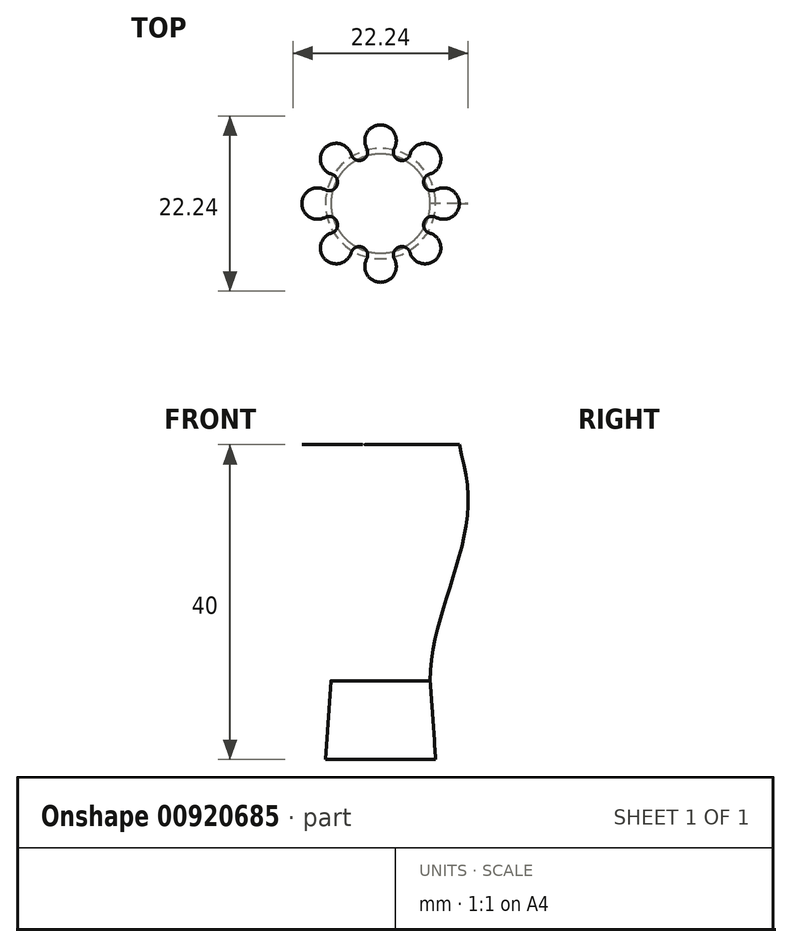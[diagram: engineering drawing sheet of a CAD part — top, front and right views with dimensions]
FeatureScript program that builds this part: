
annotation { "Feature Type Name" : "Feature", "Feature Type Description" : "" }
export const myFeature = defineFeature(function(context is Context, id is Id, definition is map)
    precondition{}
    {
        {
            var Q0;
            Q0=qCreatedBy(makeId("Front.planeOp"),FACE);
            var sketch = newSketch(context, id + "F0", { "sketchPlane" : qUnion([Q0])});
            skLineSegment(sketch, "E0", {"start": v(0, 0) * mm, "end": v(0, 33.9) * mm, "construction": true});
            skLineSegment(sketch, "E1", {"start": v(0, 0) * mm, "end": v(7, 0) * mm});
            skLineSegment(sketch, "E2", {"start": v(7, 0) * mm, "end": v(6.3, 10) * mm});
            skFitSpline(sketch, "E3", {"points": [v(6.3, 10) * mm, v(10, 40) * mm], "startDerivative": vector(-2.26, 32.38) * mm, "endDerivative": vector(-12.1, 32.97) * mm});
            skLineSegment(sketch, "E4", {"start": v(11.1, 33.89) * mm, "end": v(11.1, 17.48) * mm, "construction": true});
            skSolve(sketch);
        }
        {
            var Q0;
            Q0=qCreatedBy(makeId("Top.planeOp"),FACE);
            var Q1;
            Q1=sQuery(id+"F0.wireOp",VERTEX,"E2.end");
            cPlane(context, id + "F1", {"entities" : qUnion([Q0, Q1]), "cplaneType" : CPlaneType.PLANE_POINT, "offset" : 25 * mm, "width" : 150 * mm, "height" : 150 * mm});
        }
        {
            var Q0;
            Q0=qCreatedBy(makeId("Top.planeOp"),FACE);
            var Q1;
            Q1=sQuery(id+"F0.wireOp",VERTEX,"E4.start");
            cPlane(context, id + "F2", {"entities" : qUnion([Q0, Q1]), "cplaneType" : CPlaneType.PLANE_POINT, "offset" : 25 * mm, "width" : 150 * mm, "height" : 150 * mm});
        }
        {
            var Q0;
            Q0=qCreatedBy(makeId("Top.planeOp"),FACE);
            var Q1;
            Q1=sQuery(id+"F0.wireOp",VERTEX,"E3.end");
            cPlane(context, id + "F3", {"entities" : qUnion([Q0, Q1]), "cplaneType" : CPlaneType.PLANE_POINT, "offset" : 25 * mm, "width" : 150 * mm, "height" : 150 * mm});
        }
        {
            var Q0;
            Q0=qCreatedBy(makeId("Top.planeOp"),FACE);
            var sketch = newSketch(context, id + "F4", { "sketchPlane" : qUnion([Q0])});
            skCircle(sketch, "E5", {"center": v(0, 0) * mm, "radius": 7 * mm});
            skSolve(sketch);
        }
        {
            var Q0;
            Q0=qCreatedBy(id+"F1.planeOp",FACE);
            var sketch = newSketch(context, id + "F5", { "sketchPlane" : qUnion([Q0])});
            skCircle(sketch, "E6", {"center": v(0, 0) * mm, "radius": 6.3 * mm});
            skSolve(sketch);
        }
        {
            var Q0;
            Q0=qCreatedBy(id+"F3.planeOp",FACE);
            var sketch = newSketch(context, id + "F6", { "sketchPlane" : qUnion([Q0])});
            skCircle(sketch, "E7", {"center": v(0, 0) * mm, "radius": 10 * mm, "construction": true});
            skCircle(sketch, "E8", {"center": v(0, 0) * mm, "radius": 6 * mm, "construction": true});
            skLineSegment(sketch, "E9", {"start": v(0, 0) * mm, "end": v(12.38, 0) * mm, "construction": true});
            skLineSegment(sketch, "E10", {"start": v(0, 0) * mm, "end": v(10.76, 4.46) * mm, "construction": true});
            skArc(sketch, "E11", {"start": v(10, 0) * mm, "mid": v(9.02, 1.72) * mm, "end": v(7.05, 1.76) * mm});
            skArc(sketch, "E12", {"start": v(5.54, 2.3) * mm, "mid": v(6.18, 1.7) * mm, "end": v(7.05, 1.76) * mm});
            skArc(sketch, "E13.MirrorCS", {"start": v(5.54, -2.3) * mm, "mid": v(6.18, -1.7) * mm, "end": v(7.05, -1.76) * mm});
            skArc(sketch, "E14.MirrorCS", {"start": v(10, 0) * mm, "mid": v(9.02, -1.72) * mm, "end": v(7.05, -1.76) * mm});
            skArc(sketch, "E15.1.0", {"start": v(2.3, 5.54) * mm, "mid": v(3.17, 5.57) * mm, "end": v(3.74, 6.23) * mm});
            skArc(sketch, "E15.1.1", {"start": v(7.07, 7.07) * mm, "mid": v(5.17, 7.6) * mm, "end": v(3.74, 6.23) * mm});
            skArc(sketch, "E15.1.2", {"start": v(7.07, 7.07) * mm, "mid": v(7.6, 5.17) * mm, "end": v(6.23, 3.74) * mm});
            skArc(sketch, "E15.1.3", {"start": v(5.54, 2.3) * mm, "mid": v(5.57, 3.17) * mm, "end": v(6.23, 3.74) * mm});
            skArc(sketch, "E15.2.0", {"start": v(-2.3, 5.54) * mm, "mid": v(-1.7, 6.18) * mm, "end": v(-1.76, 7.05) * mm});
            skArc(sketch, "E15.2.1", {"start": v(0, 10) * mm, "mid": v(-1.72, 9.02) * mm, "end": v(-1.76, 7.05) * mm});
            skArc(sketch, "E15.2.2", {"start": v(0, 10) * mm, "mid": v(1.72, 9.02) * mm, "end": v(1.76, 7.05) * mm});
            skArc(sketch, "E15.2.3", {"start": v(2.3, 5.54) * mm, "mid": v(1.7, 6.18) * mm, "end": v(1.76, 7.05) * mm});
            skArc(sketch, "E15.3.0", {"start": v(-5.54, 2.3) * mm, "mid": v(-5.57, 3.17) * mm, "end": v(-6.23, 3.74) * mm});
            skArc(sketch, "E15.3.1", {"start": v(-7.07, 7.07) * mm, "mid": v(-7.6, 5.17) * mm, "end": v(-6.23, 3.74) * mm});
            skArc(sketch, "E15.3.2", {"start": v(-7.07, 7.07) * mm, "mid": v(-5.17, 7.6) * mm, "end": v(-3.74, 6.23) * mm});
            skArc(sketch, "E15.3.3", {"start": v(-2.3, 5.54) * mm, "mid": v(-3.17, 5.57) * mm, "end": v(-3.74, 6.23) * mm});
            skArc(sketch, "E15.4.0", {"start": v(-5.54, -2.3) * mm, "mid": v(-6.18, -1.7) * mm, "end": v(-7.05, -1.76) * mm});
            skArc(sketch, "E15.4.1", {"start": v(-10, 0) * mm, "mid": v(-9.02, -1.72) * mm, "end": v(-7.05, -1.76) * mm});
            skArc(sketch, "E15.4.2", {"start": v(-10, 0) * mm, "mid": v(-9.02, 1.72) * mm, "end": v(-7.05, 1.76) * mm});
            skArc(sketch, "E15.4.3", {"start": v(-5.54, 2.3) * mm, "mid": v(-6.18, 1.7) * mm, "end": v(-7.05, 1.76) * mm});
            skArc(sketch, "E15.5.0", {"start": v(-2.3, -5.54) * mm, "mid": v(-3.17, -5.57) * mm, "end": v(-3.74, -6.23) * mm});
            skArc(sketch, "E15.5.1", {"start": v(-7.07, -7.07) * mm, "mid": v(-5.17, -7.6) * mm, "end": v(-3.74, -6.23) * mm});
            skArc(sketch, "E15.5.2", {"start": v(-7.07, -7.07) * mm, "mid": v(-7.6, -5.17) * mm, "end": v(-6.23, -3.74) * mm});
            skArc(sketch, "E15.5.3", {"start": v(-5.54, -2.3) * mm, "mid": v(-5.57, -3.17) * mm, "end": v(-6.23, -3.74) * mm});
            skArc(sketch, "E15.6.0", {"start": v(2.3, -5.54) * mm, "mid": v(1.7, -6.18) * mm, "end": v(1.76, -7.05) * mm});
            skArc(sketch, "E15.6.1", {"start": v(0, -10) * mm, "mid": v(1.72, -9.02) * mm, "end": v(1.76, -7.05) * mm});
            skArc(sketch, "E15.6.2", {"start": v(0, -10) * mm, "mid": v(-1.72, -9.02) * mm, "end": v(-1.76, -7.05) * mm});
            skArc(sketch, "E15.6.3", {"start": v(-2.3, -5.54) * mm, "mid": v(-1.7, -6.18) * mm, "end": v(-1.76, -7.05) * mm});
            skArc(sketch, "E15.7.0", {"start": v(5.54, -2.3) * mm, "mid": v(5.57, -3.17) * mm, "end": v(6.23, -3.74) * mm});
            skArc(sketch, "E15.7.1", {"start": v(7.07, -7.07) * mm, "mid": v(7.6, -5.17) * mm, "end": v(6.23, -3.74) * mm});
            skArc(sketch, "E15.7.2", {"start": v(7.07, -7.07) * mm, "mid": v(5.17, -7.6) * mm, "end": v(3.74, -6.23) * mm});
            skArc(sketch, "E15.7.3", {"start": v(2.3, -5.54) * mm, "mid": v(3.17, -5.57) * mm, "end": v(3.74, -6.23) * mm});
            skSolve(sketch);
        }
        {
            var Q0;
            Q0=qCreatedBy(id+"F2.planeOp",FACE);
            var sketch = newSketch(context, id + "F7", { "sketchPlane" : qUnion([Q0])});
            skCircle(sketch, "E16", {"center": v(0, 0) * mm, "radius": 11.1 * mm, "construction": true});
            skCircle(sketch, "E17", {"center": v(0, 0) * mm, "radius": 7.1 * mm, "construction": true});
            skCircle(sketch, "E18.0", {"center": v(0, 0) * mm, "radius": 10 * mm, "construction": true});
            skCircle(sketch, "E19.0", {"center": v(0, 0) * mm, "radius": 6 * mm, "construction": true});
            skLineSegment(sketch, "E20", {"start": v(0, 10) * mm, "end": v(0, 11.1) * mm, "construction": true});
            skLineSegment(sketch, "E21", {"start": v(0, 6) * mm, "end": v(0, 7.1) * mm, "construction": true});
            skArc(sketch, "E22", {"start": v(11.1, 0) * mm, "mid": v(10.25, 1.63) * mm, "end": v(8.42, 1.88) * mm});
            skArc(sketch, "E23", {"start": v(6.55, 2.71) * mm, "mid": v(7.32, 1.93) * mm, "end": v(8.42, 1.88) * mm});
            skLineSegment(sketch, "E24.0", {"start": v(0, 0) * mm, "end": v(10.76, 4.46) * mm, "construction": true});
            skLineSegment(sketch, "E25.0", {"start": v(0, 0) * mm, "end": v(12.38, 0) * mm, "construction": true});
            skArc(sketch, "E26.MirrorCS", {"start": v(11.1, 0) * mm, "mid": v(10.25, -1.63) * mm, "end": v(8.42, -1.88) * mm});
            skArc(sketch, "E27.MirrorCS", {"start": v(6.55, -2.71) * mm, "mid": v(7.32, -1.93) * mm, "end": v(8.42, -1.88) * mm});
            skArc(sketch, "E28.1.0", {"start": v(2.71, 6.55) * mm, "mid": v(3.82, 6.54) * mm, "end": v(4.62, 7.29) * mm});
            skArc(sketch, "E28.1.1", {"start": v(7.84, 7.84) * mm, "mid": v(6.1, 8.4) * mm, "end": v(4.62, 7.29) * mm});
            skArc(sketch, "E28.1.2", {"start": v(7.84, 7.84) * mm, "mid": v(8.4, 6.1) * mm, "end": v(7.29, 4.62) * mm});
            skArc(sketch, "E28.1.3", {"start": v(6.55, 2.71) * mm, "mid": v(6.54, 3.82) * mm, "end": v(7.29, 4.62) * mm});
            skArc(sketch, "E28.2.0", {"start": v(-2.71, 6.55) * mm, "mid": v(-1.93, 7.32) * mm, "end": v(-1.88, 8.42) * mm});
            skArc(sketch, "E28.2.1", {"start": v(0, 11.1) * mm, "mid": v(-1.63, 10.25) * mm, "end": v(-1.88, 8.42) * mm});
            skArc(sketch, "E28.2.2", {"start": v(0, 11.1) * mm, "mid": v(1.63, 10.25) * mm, "end": v(1.88, 8.42) * mm});
            skArc(sketch, "E28.2.3", {"start": v(2.71, 6.55) * mm, "mid": v(1.93, 7.32) * mm, "end": v(1.88, 8.42) * mm});
            skArc(sketch, "E28.3.0", {"start": v(-6.55, 2.71) * mm, "mid": v(-6.54, 3.82) * mm, "end": v(-7.29, 4.62) * mm});
            skArc(sketch, "E28.3.1", {"start": v(-7.84, 7.84) * mm, "mid": v(-8.4, 6.1) * mm, "end": v(-7.29, 4.62) * mm});
            skArc(sketch, "E28.3.2", {"start": v(-7.84, 7.84) * mm, "mid": v(-6.1, 8.4) * mm, "end": v(-4.62, 7.29) * mm});
            skArc(sketch, "E28.3.3", {"start": v(-2.71, 6.55) * mm, "mid": v(-3.82, 6.54) * mm, "end": v(-4.62, 7.29) * mm});
            skArc(sketch, "E28.4.0", {"start": v(-6.55, -2.71) * mm, "mid": v(-7.32, -1.93) * mm, "end": v(-8.42, -1.88) * mm});
            skArc(sketch, "E28.4.1", {"start": v(-11.1, 0) * mm, "mid": v(-10.25, -1.63) * mm, "end": v(-8.42, -1.88) * mm});
            skArc(sketch, "E28.4.2", {"start": v(-11.1, 0) * mm, "mid": v(-10.25, 1.63) * mm, "end": v(-8.42, 1.88) * mm});
            skArc(sketch, "E28.4.3", {"start": v(-6.55, 2.71) * mm, "mid": v(-7.32, 1.93) * mm, "end": v(-8.42, 1.88) * mm});
            skArc(sketch, "E28.5.0", {"start": v(-2.71, -6.55) * mm, "mid": v(-3.82, -6.54) * mm, "end": v(-4.62, -7.29) * mm});
            skArc(sketch, "E28.5.1", {"start": v(-7.84, -7.84) * mm, "mid": v(-6.1, -8.4) * mm, "end": v(-4.62, -7.29) * mm});
            skArc(sketch, "E28.5.2", {"start": v(-7.84, -7.84) * mm, "mid": v(-8.4, -6.1) * mm, "end": v(-7.29, -4.62) * mm});
            skArc(sketch, "E28.5.3", {"start": v(-6.55, -2.71) * mm, "mid": v(-6.54, -3.82) * mm, "end": v(-7.29, -4.62) * mm});
            skArc(sketch, "E28.6.0", {"start": v(2.71, -6.55) * mm, "mid": v(1.93, -7.32) * mm, "end": v(1.88, -8.42) * mm});
            skArc(sketch, "E28.6.1", {"start": v(0, -11.1) * mm, "mid": v(1.63, -10.25) * mm, "end": v(1.88, -8.42) * mm});
            skArc(sketch, "E28.6.2", {"start": v(0, -11.1) * mm, "mid": v(-1.63, -10.25) * mm, "end": v(-1.88, -8.42) * mm});
            skArc(sketch, "E28.6.3", {"start": v(-2.71, -6.55) * mm, "mid": v(-1.93, -7.32) * mm, "end": v(-1.88, -8.42) * mm});
            skArc(sketch, "E28.7.0", {"start": v(6.55, -2.71) * mm, "mid": v(6.54, -3.82) * mm, "end": v(7.29, -4.62) * mm});
            skArc(sketch, "E28.7.1", {"start": v(7.84, -7.84) * mm, "mid": v(8.4, -6.1) * mm, "end": v(7.29, -4.62) * mm});
            skArc(sketch, "E28.7.2", {"start": v(7.84, -7.84) * mm, "mid": v(6.1, -8.4) * mm, "end": v(4.62, -7.29) * mm});
            skArc(sketch, "E28.7.3", {"start": v(2.71, -6.55) * mm, "mid": v(3.82, -6.54) * mm, "end": v(4.62, -7.29) * mm});
            skSolve(sketch);
        }
        {
            var Q0;
            Q0=sQuery(id+"F0.wireOp",EDGE,"E3");
            var Q1;
            Q1=sQuery(id+"F0.wireOp",EDGE,"E2");
            var Q2;
            Q2=makeQuery(id+"F6.imprint","IMPRINT",FACE,{"disambiguationData":[TD([[makeQuery(id+"F6.imprint","IMPRINT",EDGE,{"derivedFrom":sQuery(id+"F6.wireOp",EDGE,"E11")}),1.0]])]});
            var Q3;
            Q3=makeQuery(id+"F7.imprint","IMPRINT",FACE,{"disambiguationData":[TD([[makeQuery(id+"F7.imprint","IMPRINT",EDGE,{"derivedFrom":sQuery(id+"F7.wireOp",EDGE,"E22")}),1.0]])]});
            var Q4;
            Q4=makeQuery(id+"F5.imprint","IMPRINT",FACE,{"disambiguationData":[TD([[makeQuery(id+"F5.imprint","IMPRINT",EDGE,{"derivedFrom":sQuery(id+"F5.wireOp",EDGE,"E6")}),1.0]])]});
            var Q5;
            Q5=sQuery(id+"F0.wireOp",EDGE,"E2");
            var Q6;
            Q6=sQuery(id+"F0.wireOp",EDGE,"E3");
            loft(context, id + "F8", {"spine" : qUnion([Q0, Q1]), "endCondition" : LoftEndDerivativeType.NORMAL_TO_PROFILE, "endMagnitude" : 1, "sheetProfilesArray" : [{ "sheetProfileEntities" : qUnion([Q2]) }, { "sheetProfileEntities" : qUnion([Q3]) }, { "sheetProfileEntities" : qUnion([Q4]) }], "guidesArray" : [{ "guideEntities" : qUnion([Q5]), "guideDerivativeType" : LoftGuideDerivativeType.DEFAULT, "guideDerivativeMagnitude" : 1 }, { "guideEntities" : qUnion([Q6]), "guideDerivativeType" : LoftGuideDerivativeType.DEFAULT, "guideDerivativeMagnitude" : 1 }]});
        }
        {
            var Q1;
            Q1 = qSketchRegion(id + "F4", true);
            var Q2;
            Q2 = qSketchRegion(id + "F5", true);
            loft(context, id + "F9", {"operationType" : NewBodyOperationType.ADD, "sheetProfilesArray" : [{ "sheetProfileEntities" : qUnion([Q1]) }, { "sheetProfileEntities" : qUnion([Q2]) }]});
        }
    });
